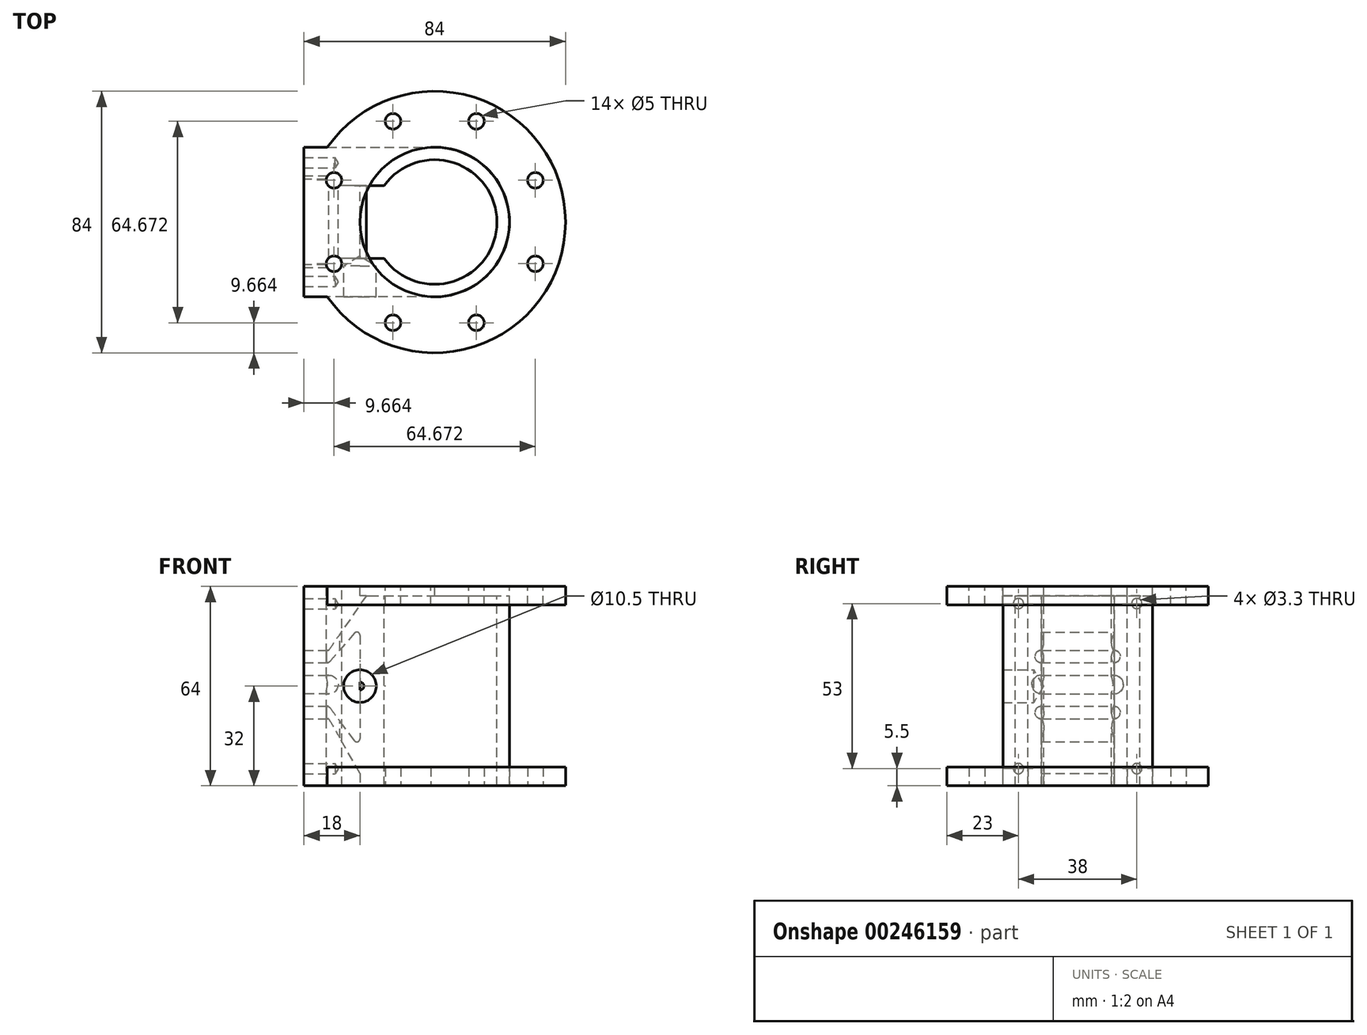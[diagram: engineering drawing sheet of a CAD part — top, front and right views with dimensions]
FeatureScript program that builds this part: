
annotation { "Feature Type Name" : "Feature", "Feature Type Description" : "" }
export const myFeature = defineFeature(function(context is Context, id is Id, definition is map)
    precondition{}
    {
        {
            var Q0;
            Q0=qCreatedBy(makeId("Top.planeOp"),FACE);
            var sketch = newSketch(context, id + "F0", { "sketchPlane" : qUnion([Q0])});
            skArc(sketch, "E0", {"start": v(-34.47, -24) * mm, "mid": v(42, 0) * mm, "end": v(-34.47, 24) * mm});
            skCircle(sketch, "E1", {"center": v(0, 0) * mm, "radius": 20 * mm});
            skCircle(sketch, "E2", {"center": v(0, 0) * mm, "radius": 35 * mm, "construction": true});
            skLineSegment(sketch, "E3", {"start": v(0, 71.76) * mm, "end": v(0, 20) * mm, "construction": true});
            skLineSegment(sketch, "E4", {"start": v(-64.72, 0) * mm, "end": v(-10.92, 0) * mm, "construction": true});
            skLineSegment(sketch, "E5", {"start": v(-12.55, 5.2) * mm, "end": v(-110.75, 45.87) * mm, "construction": true});
            skLineSegment(sketch, "E6", {"start": v(-7.65, 18.48) * mm, "end": v(-42.73, 103.16) * mm, "construction": true});
            skCircle(sketch, "E7", {"center": v(-32.34, 13.4) * mm, "radius": 2.5 * mm});
            skCircle(sketch, "E8", {"center": v(-13.4, 32.34) * mm, "radius": 2.5 * mm});
            skCircle(sketch, "E9.MirrorC", {"center": v(13.4, 32.34) * mm, "radius": 2.5 * mm});
            skCircle(sketch, "E10.MirrorC", {"center": v(32.34, 13.4) * mm, "radius": 2.5 * mm});
            skCircle(sketch, "E11.MirrorC", {"center": v(32.34, -13.4) * mm, "radius": 2.5 * mm});
            skCircle(sketch, "E12.MirrorC", {"center": v(13.4, -32.34) * mm, "radius": 2.5 * mm});
            skCircle(sketch, "E13.MirrorC", {"center": v(-13.4, -32.34) * mm, "radius": 2.5 * mm});
            skCircle(sketch, "E14.MirrorC", {"center": v(-32.34, -13.4) * mm, "radius": 2.5 * mm});
            skCircle(sketch, "E15", {"center": v(0, 0) * mm, "radius": 24 * mm});
            skLineSegment(sketch, "E16", {"start": v(0, 24) * mm, "end": v(-42, 24) * mm});
            skLineSegment(sketch, "E17", {"start": v(0, 24) * mm, "end": v(0, -24) * mm, "construction": true});
            skLineSegment(sketch, "E18", {"start": v(0, -24) * mm, "end": v(-42, -24) * mm});
            skLineSegment(sketch, "E19", {"start": v(-42, -24) * mm, "end": v(-42, 24) * mm});
            skLineSegment(sketch, "E20", {"start": v(-19.69, 3.53) * mm, "end": v(-38.39, 3.53) * mm, "construction": true});
            skLineSegment(sketch, "E21", {"start": v(-38.39, 3.53) * mm, "end": v(-38.39, -3.53) * mm, "construction": true});
            skLineSegment(sketch, "E22", {"start": v(-38.39, -3.53) * mm, "end": v(-19.69, -3.53) * mm, "construction": true});
            skPoint(sketch, "E23", {"position": v(-38.39, 0) * mm});
            skCircle(sketch, "E24", {"center": v(-20, 0) * mm, "radius": 9.08 * mm, "construction": true});
            skLineSegment(sketch, "E25.bottom", {"start": v(-42, -21) * mm, "end": v(-32.3, -21) * mm, "construction": true});
            skLineSegment(sketch, "E25.top", {"start": v(-42, -17.1) * mm, "end": v(-32.3, -17.1) * mm, "construction": true});
            skLineSegment(sketch, "E25.left", {"start": v(-42, -21) * mm, "end": v(-42, -17.1) * mm, "construction": true});
            skLineSegment(sketch, "E25.right", {"start": v(-32.3, -21) * mm, "end": v(-32.3, -17.1) * mm, "construction": true});
            skLineSegment(sketch, "E26.bottom", {"start": v(-42, 21.16) * mm, "end": v(-32.38, 21.16) * mm, "construction": true});
            skLineSegment(sketch, "E26.top", {"start": v(-42, 17.49) * mm, "end": v(-32.38, 17.49) * mm, "construction": true});
            skLineSegment(sketch, "E26.left", {"start": v(-42, 21.16) * mm, "end": v(-42, 17.49) * mm});
            skLineSegment(sketch, "E26.right", {"start": v(-32.38, 21.16) * mm, "end": v(-32.38, 17.49) * mm, "construction": true});
            skLineSegment(sketch, "E27.bottom", {"start": v(-34.59, 9.94) * mm, "end": v(-30.32, 9.94) * mm, "construction": true});
            skLineSegment(sketch, "E27.top", {"start": v(-34.59, -9.9) * mm, "end": v(-30.32, -9.9) * mm, "construction": true});
            skLineSegment(sketch, "E27.left", {"start": v(-34.59, 9.94) * mm, "end": v(-34.59, -9.9) * mm, "construction": true});
            skLineSegment(sketch, "E27.right", {"start": v(-30.32, 9.94) * mm, "end": v(-30.32, -9.9) * mm, "construction": true});
            skLineSegment(sketch, "E28.trimOffspring", {"start": v(0, 0) * mm, "end": v(0, -71.76) * mm, "construction": true});
            skLineSegment(sketch, "E29.trimOffspring", {"start": v(20, 0) * mm, "end": v(64.72, 0) * mm, "construction": true});
            skSolve(sketch);
        }
        {
            var Q0;
            Q0=qCreatedBy(makeId("Front.planeOp"),FACE);
            var sketch = newSketch(context, id + "F1", { "sketchPlane" : qUnion([Q0])});
            skLineSegment(sketch, "E30.bottom", {"start": v(-42, 0) * mm, "end": v(42, 0) * mm, "construction": true});
            skLineSegment(sketch, "E30.top", {"start": v(-42, -64) * mm, "end": v(42, -64) * mm, "construction": true});
            skLineSegment(sketch, "E30.left", {"start": v(-42, 0) * mm, "end": v(-42, -64) * mm, "construction": true});
            skLineSegment(sketch, "E30.right", {"start": v(42, 0) * mm, "end": v(42, -64) * mm, "construction": true});
            skLineSegment(sketch, "E31.bottom", {"start": v(-42, 0) * mm, "end": v(42, 0) * mm});
            skLineSegment(sketch, "E31.top", {"start": v(-42, -6) * mm, "end": v(42, -6) * mm});
            skLineSegment(sketch, "E31.left", {"start": v(-42, 0) * mm, "end": v(-42, -6) * mm});
            skLineSegment(sketch, "E31.right", {"start": v(42, 0) * mm, "end": v(42, -6) * mm});
            skLineSegment(sketch, "E32.bottom", {"start": v(-42, -58) * mm, "end": v(42, -58) * mm});
            skLineSegment(sketch, "E32.top", {"start": v(-42, -64) * mm, "end": v(42, -64) * mm});
            skLineSegment(sketch, "E32.left", {"start": v(-42, -58) * mm, "end": v(-42, -64) * mm});
            skLineSegment(sketch, "E32.right", {"start": v(42, -58) * mm, "end": v(42, -64) * mm});
            skLineSegment(sketch, "E33", {"start": v(-24, 0) * mm, "end": v(24, 0) * mm});
            skLineSegment(sketch, "E34", {"start": v(-24, 0) * mm, "end": v(-24, -64) * mm, "construction": true});
            skLineSegment(sketch, "E35", {"start": v(24, 0) * mm, "end": v(24, -64) * mm, "construction": true});
            skLineSegment(sketch, "E36", {"start": v(-20, 0) * mm, "end": v(-20, -64) * mm, "construction": true});
            skLineSegment(sketch, "E37", {"start": v(20.03, 0) * mm, "end": v(20.03, -58) * mm, "construction": true});
            skSolve(sketch);
        }
        {
            var Q0;
            Q0=makeQuery(id+"F0.imprint","IMPRINT",FACE,{"disambiguationData":[TD([[makeQuery(id+"F0.imprint","IMPRINT",EDGE,{"derivedFrom":sQuery(id+"F0.wireOp",EDGE,"E1")}),-1.0]])]});
            var Q1;
            Q1=makeQuery(id+"F0.imprint","IMPRINT",FACE,{"disambiguationData":[TD([[makeQuery(id+"F0.imprint","IMPRINT",EDGE,{"derivedFrom":sQuery(id+"F0.wireOp",EDGE,"E7")}),-1.0]])]});
            extrude(context, id + "F2", {"entities" : qUnion([Q0, Q1]), "oppositeDirection" : true, "depth" : 64 * mm});
        }
        {
            var Q0;
            Q0=qCreatedBy(makeId("Top.planeOp"),FACE);
            var sketch = newSketch(context, id + "F3", { "sketchPlane" : qUnion([Q0])});
            skArc(sketch, "E38", {"start": v(-34.47, -24) * mm, "mid": v(42, 0) * mm, "end": v(-34.47, 24) * mm});
            skLineSegment(sketch, "E39", {"start": v(-20, 0) * mm, "end": v(-20, 0) * mm});
            skLineSegment(sketch, "E40", {"start": v(-142.95, 0) * mm, "end": v(-116.62, 0) * mm, "construction": true});
            skCircle(sketch, "E41", {"center": v(-32.34, 13.4) * mm, "radius": 2.5 * mm});
            skCircle(sketch, "E42", {"center": v(-13.4, 32.34) * mm, "radius": 2.5 * mm});
            skCircle(sketch, "E43.MirrorC", {"center": v(13.4, 32.34) * mm, "radius": 2.5 * mm});
            skCircle(sketch, "E44.MirrorC", {"center": v(32.34, 13.4) * mm, "radius": 2.5 * mm});
            skCircle(sketch, "E45.MirrorC", {"center": v(32.34, -13.4) * mm, "radius": 2.5 * mm});
            skCircle(sketch, "E46.MirrorC", {"center": v(13.4, -32.34) * mm, "radius": 2.5 * mm});
            skCircle(sketch, "E47.MirrorC", {"center": v(-13.4, -32.34) * mm, "radius": 2.5 * mm});
            skCircle(sketch, "E48.MirrorC", {"center": v(-32.34, -13.4) * mm, "radius": 2.5 * mm});
            skLineSegment(sketch, "E49", {"start": v(0, 24) * mm, "end": v(0, 24) * mm});
            skLineSegment(sketch, "E50", {"start": v(-34.47, -24) * mm, "end": v(-42, -24) * mm});
            skLineSegment(sketch, "E51", {"start": v(-42, -24) * mm, "end": v(-42, 24) * mm});
            skLineSegment(sketch, "E52", {"start": v(-116.62, 3.53) * mm, "end": v(-116.62, -3.53) * mm, "construction": true});
            skPoint(sketch, "E53", {"position": v(-116.62, 0) * mm});
            skLineSegment(sketch, "E54.left", {"start": v(-42, -2.64) * mm, "end": v(-42, 1.25) * mm, "construction": true});
            skLineSegment(sketch, "E55.bottom", {"start": v(-112.82, 28.3) * mm, "end": v(-108.56, 28.3) * mm, "construction": true});
            skLineSegment(sketch, "E55.top", {"start": v(-112.82, 8.44) * mm, "end": v(-108.56, 8.44) * mm, "construction": true});
            skLineSegment(sketch, "E55.left", {"start": v(-112.82, 28.3) * mm, "end": v(-112.82, 8.44) * mm, "construction": true});
            skLineSegment(sketch, "E55.right", {"start": v(-108.56, 28.3) * mm, "end": v(-108.56, 8.44) * mm, "construction": true});
            skPoint(sketch, "E56.orphan", {"position": v(0, 53.4) * mm});
            skLineSegment(sketch, "E57.trimOffspring", {"start": v(0, -42) * mm, "end": v(0, -53.4) * mm, "construction": true});
            skLineSegment(sketch, "E58.trimOffspring", {"start": v(-34.47, 24) * mm, "end": v(-42, 24) * mm});
            skPoint(sketch, "E59.trimOffspring.end.orphan", {"position": v(142.95, 0) * mm});
            skCircle(sketch, "E60", {"center": v(0, 0) * mm, "radius": 24.03 * mm});
            skSolve(sketch);
        }
        {
            var Q0;
            Q0=makeQuery(id+"F3.imprint","IMPRINT",FACE,{"disambiguationData":[TD([[makeQuery(id+"F3.imprint","IMPRINT",EDGE,{"derivedFrom":sQuery(id+"F3.wireOp",EDGE,"E38")}),1.0]])]});
            extrude(context, id + "F4", {"entities" : qUnion([Q0]), "operationType" : NewBodyOperationType.ADD, "oppositeDirection" : true, "depth" : 6 * mm});
        }
        {
            var Q0;
            Q0=makeQuery(id+"F2.opExtrude","CAP_FACE",FACE,{"disambiguationData":[OSD([sQuery(id+"F0.wireOp",EDGE,"E1"),sQuery(id+"F0.wireOp",EDGE,"E15")])],"isStart":false});
            var sketch = newSketch(context, id + "F5", { "sketchPlane" : qUnion([Q0])});
            skArc(sketch, "E61.0", {"start": v(0, 24) * mm, "mid": v(24, 0) * mm, "end": v(0, -24) * mm});
            skLineSegment(sketch, "E61.1.0", {"start": v(-1.29, -24) * mm, "end": v(-34.47, -24) * mm});
            skArc(sketch, "E61.1.1", {"start": v(-34.47, -24) * mm, "mid": v(42, 0) * mm, "end": v(-34.47, 24) * mm});
            skLineSegment(sketch, "E61.1.2", {"start": v(-34.47, 24) * mm, "end": v(-1.29, 24) * mm});
            skArc(sketch, "E61.1.3", {"start": v(-1.29, 24) * mm, "mid": v(24.03, 0) * mm, "end": v(-1.29, -24) * mm});
            skCircle(sketch, "E62.0", {"center": v(13.4, 32.34) * mm, "radius": 2.5 * mm});
            skCircle(sketch, "E62.1", {"center": v(-13.4, 32.34) * mm, "radius": 2.5 * mm});
            skCircle(sketch, "E62.3", {"center": v(32.34, 13.4) * mm, "radius": 2.5 * mm});
            skCircle(sketch, "E62.4", {"center": v(32.34, -13.4) * mm, "radius": 2.5 * mm});
            skCircle(sketch, "E62.5", {"center": v(13.4, -32.34) * mm, "radius": 2.5 * mm});
            skCircle(sketch, "E62.7", {"center": v(-13.4, -32.34) * mm, "radius": 2.5 * mm});
            skSolve(sketch);
        }
        {
            var Q0;
            Q0=makeQuery(id+"F5.imprint","IMPRINT",FACE,{"disambiguationData":[TD([[makeQuery(id+"F5.imprint","IMPRINT",EDGE,{"derivedFrom":sQuery(id+"F5.wireOp",EDGE,"E61.1.0")}),1.0]])]});
            extrude(context, id + "F6", {"entities" : qUnion([Q0]), "operationType" : NewBodyOperationType.ADD, "oppositeDirection" : true, "depth" : 6 * mm});
        }
        {
            var Q0;
            Q0=makeQuery(id+"F2.opExtrude","SWEPT_FACE",FACE,{"disambiguationData":[OSD([sQuery(id+"F0.wireOp",EDGE,"E18")])]});
            var sketch = newSketch(context, id + "F7", { "sketchPlane" : qUnion([Q0])});
            skPoint(sketch, "E63.0", {"position": v(-24, -32) * mm});
            skSolve(sketch);
        }
        {
            var Q0;
            Q0=makeQuery(id+"F2.opExtrude","SWEPT_FACE",FACE,{"disambiguationData":[OSD([sQuery(id+"F0.wireOp",EDGE,"E19"),sQuery(id+"F0.wireOp",EDGE,"E26.left")])]});
            var sketch = newSketch(context, id + "F8", { "sketchPlane" : qUnion([Q0])});
            skCircle(sketch, "E64", {"center": v(-19, -5.5) * mm, "radius": 2.65 * mm});
            skCircle(sketch, "E65.MirrorC", {"center": v(19, -5.5) * mm, "radius": 2.65 * mm});
            skLineSegment(sketch, "E66", {"start": v(0, 0) * mm, "end": v(0, -64) * mm, "construction": true});
            skLineSegment(sketch, "E67", {"start": v(60.89, -32) * mm, "end": v(-49.42, -32) * mm, "construction": true});
            skPoint(sketch, "E67.startSnap0", {"position": v(0, -32) * mm});
            skCircle(sketch, "E68.MirrorC", {"center": v(-19, -58.5) * mm, "radius": 2.65 * mm});
            skCircle(sketch, "E69.MirrorC", {"center": v(19, -58.5) * mm, "radius": 2.65 * mm});
            skSolve(sketch);
        }
        {
            var Q0;
            Q0=sQuery(id+"F8.wireOp",VERTEX,"E64.center");
            var Q1;
            Q1=sQuery(id+"F8.wireOp",VERTEX,"E65.MirrorC.center");
            var Q2;
            Q2=sQuery(id+"F8.wireOp",VERTEX,"E68.MirrorC.center");
            var Q3;
            Q3=sQuery(id+"F8.wireOp",VERTEX,"E69.MirrorC.center");
            var Q4;
            Q4=makeQuery(id+"F2.opExtrude","SWEPT_BODY",BODY,{"disambiguationData":[OSD([sQuery(id+"F0.wireOp",EDGE,"E1"),sQuery(id+"F0.wireOp",EDGE,"E7"),sQuery(id+"F0.wireOp",EDGE,"E14.MirrorC"),sQuery(id+"F0.wireOp",EDGE,"E15"),sQuery(id+"F0.wireOp",EDGE,"E16"),sQuery(id+"F0.wireOp",EDGE,"E18"),sQuery(id+"F0.wireOp",EDGE,"E19"),sQuery(id+"F0.wireOp",EDGE,"E26.left")])]});
            hole(context, id + "F9", {"style" : HoleStyle.SIMPLE, "endStyle" : HoleEndStyle.BLIND, "holeDiameter" : 3.3 * mm, "holeDepth" : 10 * mm, "tappedDepth" : 12.7 * mm, "tapClearance" : 3, "locations" : qUnion([Q0, Q1, Q2, Q3]), "scope" : qUnion([Q4]), "startStyle" : HoleStartStyle.PART});
        }
        {
            var Q0;
            Q0=makeQuery(id+"F0.imprint","IMPRINT",FACE,{"disambiguationData":[TD([[makeQuery(id+"F0.imprint","IMPRINT",EDGE,{"derivedFrom":sQuery(id+"F0.wireOp",EDGE,"E1")}),-1.0]])]});
            extrude(context, id + "F10", {"entities" : qUnion([Q0]), "operationType" : NewBodyOperationType.REMOVE, "oppositeDirection" : true, "depth" : 3 * mm});
        }
        {
            var Q0;
            Q0=qCreatedBy(makeId("Front.planeOp"),FACE);
            cPlane(context, id + "F11", {"entities" : qUnion([Q0]), "cplaneType" : CPlaneType.OFFSET, "offset" : 55.7 * mm, "oppositeDirection" : true, "width" : 150 * mm, "height" : 150 * mm});
        }
        {
            var Q0;
            Q0=qCreatedBy(id+"F11.planeOp",FACE);
            var sketch = newSketch(context, id + "F12", { "sketchPlane" : qUnion([Q0])});
            skLineSegment(sketch, "E70.bottom", {"start": v(-63.22, 16.05) * mm, "end": v(57.63, 16.05) * mm});
            skLineSegment(sketch, "E70.top", {"start": v(-63.22, -69.82) * mm, "end": v(57.63, -69.82) * mm});
            skLineSegment(sketch, "E70.left", {"start": v(-63.22, 16.05) * mm, "end": v(-63.22, -69.82) * mm});
            skLineSegment(sketch, "E70.right", {"start": v(57.63, 16.05) * mm, "end": v(57.63, -69.82) * mm});
            skSolve(sketch);
        }
        {
            var Q0;
            Q0=makeQuery(id+"F12.imprint","IMPRINT",FACE,{"disambiguationData":[TD([[makeQuery(id+"F12.imprint","IMPRINT",EDGE,{"derivedFrom":sQuery(id+"F12.wireOp",EDGE,"E70.bottom")}),-1.0]])]});
            extrude(context, id + "F13", {"entities" : qUnion([Q0]), "operationType" : NewBodyOperationType.REMOVE, "depth" : 55.4 * mm});
        }
        {
            var Q0;
            {var subQ4=sQuery(id+"F0.wireOp",EDGE,"E15");Q0=makeQuery(id+"F13.boolean.opBoolean","COPY",FACE,{"disambiguationData":[TD([makeQuery(id+"F10.boolean.opBoolean","COPY",FACE,{"derivedFrom":makeQuery(id+"F10.opExtrude","SWEPT_FACE",FACE,{"disambiguationData":[OSD([subQ4])]})})])],"derivedFrom":makeQuery(id+"F13.opExtrude","CAP_FACE",FACE,{"disambiguationData":[OSD([sQuery(id+"F12.wireOp",EDGE,"E70.bottom"),sQuery(id+"F12.wireOp",EDGE,"E70.top"),sQuery(id+"F12.wireOp",EDGE,"E70.left"),sQuery(id+"F12.wireOp",EDGE,"E70.right")])],"isStart":false})});}
            var sketch = newSketch(context, id + "F14", { "sketchPlane" : qUnion([Q0])});
            skLineSegment(sketch, "E71", {"start": v(24, -15.66) * mm, "end": v(24, -48.92) * mm});
            skLineSegment(sketch, "E72", {"start": v(42, -28.5) * mm, "end": v(34, -28.5) * mm});
            skLineSegment(sketch, "E73", {"start": v(34, -28.5) * mm, "end": v(34, -34.5) * mm, "construction": true});
            skLineSegment(sketch, "E74", {"start": v(34, -34.5) * mm, "end": v(42, -34.5) * mm});
            skLineSegment(sketch, "E75", {"start": v(24, -60) * mm, "end": v(24, -64) * mm});
            skArc(sketch, "E76", {"start": v(34, -28.5) * mm, "mid": v(31, -31.5) * mm, "end": v(34, -34.5) * mm});
            skLineSegment(sketch, "E77.bottom", {"start": v(42, -20.5) * mm, "end": v(34, -20.5) * mm});
            skLineSegment(sketch, "E77.top", {"start": v(42, -24.5) * mm, "end": v(34.46, -24.5) * mm});
            skLineSegment(sketch, "E77.left", {"start": v(42, -20.5) * mm, "end": v(42, -24.5) * mm});
            skLineSegment(sketch, "E77.right", {"start": v(34, -20.5) * mm, "end": v(34, -24.5) * mm, "construction": true});
            skLineSegment(sketch, "E78.bottom", {"start": v(42, -38.5) * mm, "end": v(34.5, -38.5) * mm});
            skLineSegment(sketch, "E78.top", {"start": v(42, -42.5) * mm, "end": v(34, -42.5) * mm});
            skLineSegment(sketch, "E78.left", {"start": v(42, -38.5) * mm, "end": v(42, -42.5) * mm});
            skLineSegment(sketch, "E78.right", {"start": v(34, -38.5) * mm, "end": v(34, -42.5) * mm, "construction": true});
            skLineSegment(sketch, "E79", {"start": v(22, -3) * mm, "end": v(34, -20.5) * mm});
            skLineSegment(sketch, "E80", {"start": v(24, -60) * mm, "end": v(34, -42.5) * mm});
            skLineSegment(sketch, "E81", {"start": v(25.75, -15) * mm, "end": v(33.7, -24.16) * mm});
            skLineSegment(sketch, "E82", {"start": v(25.8, -49.52) * mm, "end": v(33.7, -38.9) * mm});
            skPoint(sketch, "E83.visualSharp", {"position": v(24, -12.99) * mm});
            skArc(sketch, "E83.filletArc", {"start": v(25.75, -15) * mm, "mid": v(24.65, -14.73) * mm, "end": v(24, -15.66) * mm});
            skPoint(sketch, "E84.visualSharp", {"position": v(24, -51.94) * mm});
            skArc(sketch, "E84.filletArc", {"start": v(24, -48.92) * mm, "mid": v(24.68, -49.87) * mm, "end": v(25.8, -49.52) * mm});
            skPoint(sketch, "E85.visualSharp", {"position": v(34, -24.5) * mm});
            skArc(sketch, "E85.filletArc", {"start": v(33.7, -24.16) * mm, "mid": v(34.04, -24.4) * mm, "end": v(34.46, -24.5) * mm});
            skPoint(sketch, "E86.visualSharp", {"position": v(34, -38.5) * mm});
            skArc(sketch, "E86.filletArc", {"start": v(34.5, -38.5) * mm, "mid": v(34.05, -38.6) * mm, "end": v(33.7, -38.9) * mm});
            skLineSegment(sketch, "E87", {"start": v(22, -3) * mm, "end": v(20, -3) * mm});
            skLineSegment(sketch, "E88", {"start": v(20, -64) * mm, "end": v(24, -64) * mm});
            skLineSegment(sketch, "E89", {"start": v(42, -42.5) * mm, "end": v(42, -20.5) * mm});
            skLineSegment(sketch, "E90", {"start": v(16.24, -3) * mm, "end": v(16.24, -64) * mm});
            skLineSegment(sketch, "E91", {"start": v(16.24, -3) * mm, "end": v(20, -3) * mm});
            skLineSegment(sketch, "E92", {"start": v(16.24, -64) * mm, "end": v(20, -64) * mm});
            skSolve(sketch);
        }
        {
            var Q0;
            Q0=makeQuery(id+"F14.imprint","IMPRINT",FACE,{"disambiguationData":[TD([[makeQuery(id+"F14.imprint","IMPRINT",EDGE,{"derivedFrom":sQuery(id+"F14.wireOp",EDGE,"E71")}),-1.0]])]});
            var Q1;
            {var subQ0=sQuery(id+"F14.wireOp",EDGE,"E72");Q1=makeQuery(id+"F14.imprint","IMPRINT",FACE,{"disambiguationData":[TD([[makeQuery(id+"F14.imprint","IMPRINT",EDGE,{"derivedFrom":subQ0}),1.0]])]});}
            var Q2;
            Q2=makeQuery(id+"F14.imprint","IMPRINT",FACE,{"disambiguationData":[TD([[makeQuery(id+"F14.imprint","IMPRINT",EDGE,{"derivedFrom":sQuery(id+"F14.wireOp",EDGE,"E90")}),1.0]])]});
            extrude(context, id + "F15", {"entities" : qUnion([Q0, Q1, Q2]), "operationType" : NewBodyOperationType.REMOVE, "oppositeDirection" : true, "depth" : 12 * mm});
        }
        {
            var Q0;
            Q0=makeQuery(id+"F2.opExtrude","SWEPT_BODY",BODY,{"disambiguationData":[OSD([sQuery(id+"F0.wireOp",EDGE,"E1"),sQuery(id+"F0.wireOp",EDGE,"E7"),sQuery(id+"F0.wireOp",EDGE,"E14.MirrorC"),sQuery(id+"F0.wireOp",EDGE,"E15"),sQuery(id+"F0.wireOp",EDGE,"E16"),sQuery(id+"F0.wireOp",EDGE,"E18"),sQuery(id+"F0.wireOp",EDGE,"E19"),sQuery(id+"F0.wireOp",EDGE,"E26.left")])]});
            var Q1;
            Q1=qCreatedBy(makeId("Front.planeOp"),FACE);
            mirror(context, id + "F16", {"operationType" : NewBodyOperationType.ADD, "entities" : qUnion([Q0]), "mirrorPlane" : qUnion([Q1])});
        }
        {
            var Q0;
            Q0=sQuery(id+"F7.wireOp",VERTEX,"E63.0");
            var Q1;
            Q1=makeQuery(id+"F2.opExtrude","SWEPT_BODY",BODY,{"disambiguationData":[OSD([sQuery(id+"F0.wireOp",EDGE,"E1"),sQuery(id+"F0.wireOp",EDGE,"E7"),sQuery(id+"F0.wireOp",EDGE,"E14.MirrorC"),sQuery(id+"F0.wireOp",EDGE,"E15"),sQuery(id+"F0.wireOp",EDGE,"E16"),sQuery(id+"F0.wireOp",EDGE,"E18"),sQuery(id+"F0.wireOp",EDGE,"E19"),sQuery(id+"F0.wireOp",EDGE,"E26.left")])]});
            hole(context, id + "F17", {"style" : HoleStyle.SIMPLE, "endStyle" : HoleEndStyle.BLIND, "holeDiameter" : 10.5 * mm, "holeDepth" : 9.9 * mm, "tappedDepth" : 12.7 * mm, "tapClearance" : 3, "locations" : qUnion([Q0]), "scope" : qUnion([Q1]), "startStyle" : HoleStartStyle.PART});
        }
        {
            var Q0;
            {var subQ0=makeQuery(id+"F2.opExtrude","SWEPT_FACE",FACE,{"disambiguationData":[OSD([sQuery(id+"F0.wireOp",EDGE,"E19"),sQuery(id+"F0.wireOp",EDGE,"E26.left")])]});Q0=makeQuery(id+"F16.boolean.opBoolean","MERGE",FACE,{"derivedFrom":[subQ0,makeQuery(id+"F16.opPattern","COPY",FACE,{"derivedFrom":subQ0,"instanceName":"1"})]});}
            var sketch = newSketch(context, id + "F18", { "sketchPlane" : qUnion([Q0])});
            skArc(sketch, "E93", {"start": v(-11.7, -20.5) * mm, "mid": v(-13.7, -22.5) * mm, "end": v(-11.7, -24.5) * mm});
            skArc(sketch, "E94", {"start": v(11.7, -24.5) * mm, "mid": v(13.7, -22.5) * mm, "end": v(11.7, -20.5) * mm});
            skArc(sketch, "E95", {"start": v(11.7, -34.5) * mm, "mid": v(14.7, -31.5) * mm, "end": v(11.7, -28.5) * mm});
            skArc(sketch, "E96", {"start": v(-11.7, -28.5) * mm, "mid": v(-14.7, -31.5) * mm, "end": v(-11.7, -34.5) * mm});
            skArc(sketch, "E97", {"start": v(-11.7, -38.5) * mm, "mid": v(-13.7, -40.5) * mm, "end": v(-11.7, -42.5) * mm});
            skArc(sketch, "E98", {"start": v(11.7, -42.5) * mm, "mid": v(13.7, -40.5) * mm, "end": v(11.7, -38.5) * mm});
            skLineSegment(sketch, "E99", {"start": v(-11.7, -28.5) * mm, "end": v(11.7, -28.5) * mm});
            skLineSegment(sketch, "E100", {"start": v(11.7, -34.5) * mm, "end": v(-11.7, -34.5) * mm});
            skLineSegment(sketch, "E101", {"start": v(-11.7, -38.5) * mm, "end": v(11.7, -38.5) * mm});
            skLineSegment(sketch, "E102", {"start": v(11.7, -42.5) * mm, "end": v(-11.7, -42.5) * mm});
            skLineSegment(sketch, "E103", {"start": v(-11.7, -34.5) * mm, "end": v(11.7, -34.5) * mm});
            skLineSegment(sketch, "E104", {"start": v(-11.7, -24.5) * mm, "end": v(11.7, -24.5) * mm});
            skLineSegment(sketch, "E105", {"start": v(-11.7, -20.5) * mm, "end": v(11.7, -20.5) * mm});
            skSolve(sketch);
        }
        {
            var Q0;
            Q0=makeQuery(id+"F18.imprint","IMPRINT",FACE,{"disambiguationData":[TD([[makeQuery(id+"F18.imprint","IMPRINT",EDGE,{"derivedFrom":sQuery(id+"F18.wireOp",EDGE,"E93")}),1.0]])]});
            var Q1;
            Q1=makeQuery(id+"F18.imprint","IMPRINT",FACE,{"disambiguationData":[TD([[makeQuery(id+"F18.imprint","IMPRINT",EDGE,{"derivedFrom":sQuery(id+"F18.wireOp",EDGE,"E94")}),1.0]])]});
            var Q2;
            Q2=makeQuery(id+"F18.imprint","IMPRINT",FACE,{"disambiguationData":[TD([[makeQuery(id+"F18.imprint","IMPRINT",EDGE,{"derivedFrom":sQuery(id+"F18.wireOp",EDGE,"E96")}),1.0]])]});
            var Q3;
            Q3=makeQuery(id+"F18.imprint","IMPRINT",FACE,{"disambiguationData":[TD([[makeQuery(id+"F18.imprint","IMPRINT",EDGE,{"derivedFrom":sQuery(id+"F18.wireOp",EDGE,"E95")}),1.0]])]});
            var Q4;
            Q4=makeQuery(id+"F18.imprint","IMPRINT",FACE,{"disambiguationData":[TD([[makeQuery(id+"F18.imprint","IMPRINT",EDGE,{"derivedFrom":sQuery(id+"F18.wireOp",EDGE,"E97")}),1.0]])]});
            var Q5;
            Q5=makeQuery(id+"F18.imprint","IMPRINT",FACE,{"disambiguationData":[TD([[makeQuery(id+"F18.imprint","IMPRINT",EDGE,{"derivedFrom":sQuery(id+"F18.wireOp",EDGE,"E98")}),1.0]])]});
            extrude(context, id + "F19", {"entities" : qUnion([Q0, Q1, Q2, Q3, Q4, Q5]), "operationType" : NewBodyOperationType.REMOVE, "oppositeDirection" : true, "depth" : 10 * mm});
        }
    });
